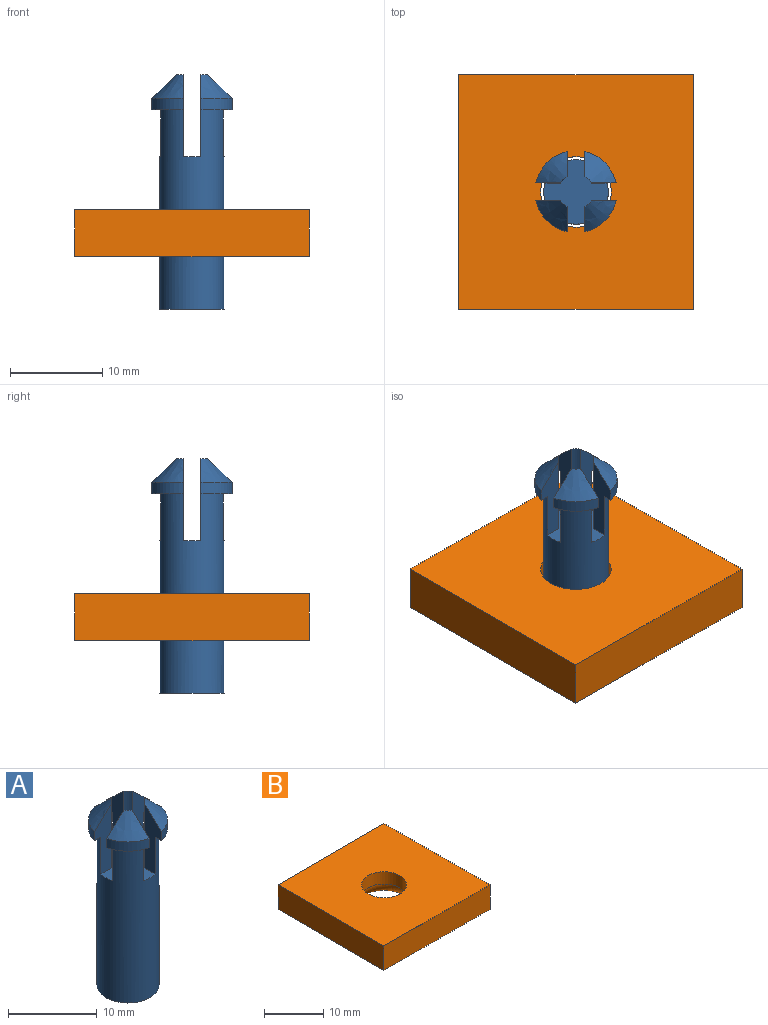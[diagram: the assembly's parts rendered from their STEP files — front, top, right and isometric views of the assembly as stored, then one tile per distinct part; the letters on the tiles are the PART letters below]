
ASSEMBLY  parts=2 mates=1
PART A: 27 faces, bbox 9.1x9.1x25.8 mm
  f0: cylinder r=4.45mm len=3.39mm, axis (0,0,-1), area 6.4mm2, adj f4,f7,f15,f16
  f1: cylinder r=4.45mm len=3.39mm, axis (0,0,-1), area 6.4mm2, adj f5,f8,f17,f18
  f2: cylinder r=4.45mm len=3.39mm, axis (0,0,-1), area 6.4mm2, adj f6,f9,f19,f20
  f3: cylinder r=3.49mm len=21.59mm, axis (0,0,-1), area 434.6mm2, adj f4,f5,f6,f11,f12,f14,f15,f16
  f4: plane 3.39x3.39mm, normal (0,0,-1), area 4.1mm2, adj f0,f3,f15,f16
  f5: plane 3.39x3.39mm, normal (0,0,-1), area 4.1mm2, adj f1,f3,f17,f18
  f6: plane 3.39x3.39mm, normal (0,0,-1), area 4.1mm2, adj f2,f3,f19,f20
  f7: cone r=1.91mm half-angle=45deg, axis (0,0,-1), area 9.9mm2, adj f0,f15,f16,f26
  f8: cone r=1.91mm half-angle=45deg, axis (0,0,-1), area 9.9mm2, adj f1,f17,f18,f25
  f9: cone r=1.91mm half-angle=45deg, axis (0,0,-1), area 9.9mm2, adj f2,f19,f20,f24
  f10: cylinder r=4.45mm len=3.39mm, axis (0,0,-1), area 6.4mm2, adj f11,f13,f21,f22
  f11: plane 3.39x3.39mm, normal (0,0,-1), area 4.1mm2, adj f3,f10,f21,f22
  f12: plane 6.99x6.99mm, normal (0,0,-1), area 38.3mm2, adj f3
  f13: cone r=1.91mm half-angle=45deg, axis (0,0,-1), area 9.9mm2, adj f10,f21,f22,f23
  f14: plane 6.99x6.99mm, normal (0,0,1), area 23.8mm2, adj f3,f15,f16,f17,f18,f19,f20,f21
  f15: plane 9.29x3.1mm, normal (0,-1,0), area 15.6mm2, adj f0,f3,f4,f7,f14,f26
  f16: plane 9.29x3.1mm, normal (-1,0,0), area 15.6mm2, adj f0,f3,f4,f7,f14,f26
  f17: plane 9.29x3.1mm, normal (1,0,0), area 15.6mm2, adj f1,f3,f5,f8,f14,f25
  f18: plane 9.29x3.1mm, normal (0,-1,0), area 15.6mm2, adj f1,f3,f5,f8,f14,f25
  f19: plane 9.29x3.1mm, normal (0,1,0), area 15.6mm2, adj f2,f3,f6,f9,f14,f24
  f20: plane 9.29x3.1mm, normal (1,0,0), area 15.6mm2, adj f2,f3,f6,f9,f14,f24
  f21: plane 9.29x3.1mm, normal (-1,0,0), area 15.6mm2, adj f3,f10,f11,f13,f14,f23
  f22: plane 9.29x3.1mm, normal (0,1,0), area 15.6mm2, adj f3,f10,f11,f13,f14,f23
  f23: cylinder r=1.91mm len=8.89mm, axis (0,0,1), area 8.9mm2, adj f13,f14,f21,f22
  f24: cylinder r=1.91mm len=8.89mm, axis (0,0,1), area 8.9mm2, adj f9,f14,f19,f20
  f25: cylinder r=1.91mm len=8.89mm, axis (0,0,1), area 8.9mm2, adj f8,f14,f17,f18
  f26: cylinder r=1.91mm len=8.89mm, axis (0,0,1), area 8.9mm2, adj f7,f14,f15,f16
PART B: 8 faces, bbox 25.4x25.4x5.1 mm
  f0: plane 25.4x5.08mm, normal (0,-1,0), area 129mm2, adj f1,f4,f5,f6
  f1: plane 25.4x5.08mm, normal (1,0,0), area 129mm2, adj f0,f2,f5,f6
  f2: plane 25.4x5.08mm, normal (0,1,0), area 129mm2, adj f1,f4,f5,f6
  f3: cylinder r=3.81mm len=7.62mm, axis (0,0,-1), area 60.8mm2, adj f5,f7
  f4: plane 25.4x5.08mm, normal (-1,0,0), area 129mm2, adj f0,f2,f5,f6
  f5: plane 25.4x25.4mm, normal (0,0,1), area 599.6mm2, adj f0,f1,f2,f3,f4
  f6: plane 25.4x25.4mm, normal (0,0,-1), area 518.5mm2, adj f0,f1,f2,f4,f7
  f7: torus R=6.35mm, axis (0,0,1), area 118.7mm2, adj f3,f6
PLACE A t=(7.03,12.25,4.02)mm
PLACE B t=(19.73,-0.45,9.74)mm
MATE pin_slot A.f3 <-> B.f3  axis (0,0,-1) through (7.03,12.25,14.82)mm
